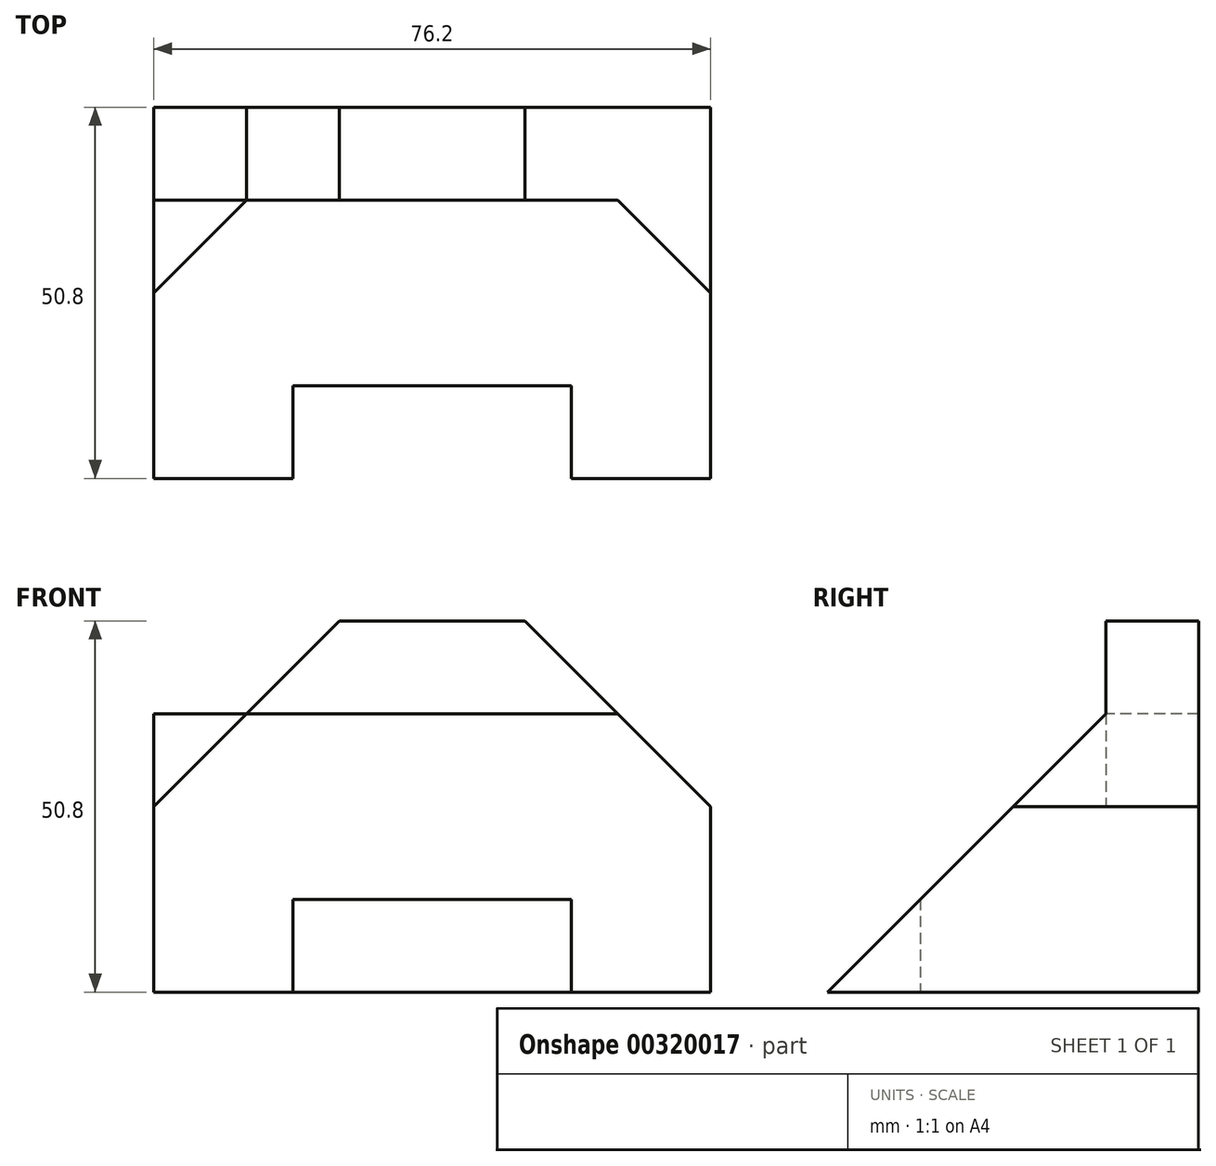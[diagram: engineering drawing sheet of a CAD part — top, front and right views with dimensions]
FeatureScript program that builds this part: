
annotation { "Feature Type Name" : "Feature", "Feature Type Description" : "" }
export const myFeature = defineFeature(function(context is Context, id is Id, definition is map)
    precondition{}
    {
        {
            var Q0;
            Q0=qCreatedBy(makeId("Top.planeOp"),FACE);
            var sketch = newSketch(context, id + "F0", { "sketchPlane" : qUnion([Q0])});
            skLineSegment(sketch, "E0", {"start": v(-38.1, 50.8) * mm, "end": v(-38.1, 0) * mm});
            skLineSegment(sketch, "E1", {"start": v(-38.1, 0) * mm, "end": v(-19.05, 0) * mm});
            skLineSegment(sketch, "E2", {"start": v(-19.05, 0) * mm, "end": v(-19.05, 12.7) * mm});
            skLineSegment(sketch, "E3", {"start": v(-19.05, 12.7) * mm, "end": v(19.05, 12.7) * mm});
            skLineSegment(sketch, "E4", {"start": v(19.05, 12.7) * mm, "end": v(19.05, 0) * mm});
            skLineSegment(sketch, "E5", {"start": v(19.05, 0) * mm, "end": v(38.1, 0) * mm});
            skLineSegment(sketch, "E6", {"start": v(38.1, 0) * mm, "end": v(38.1, 50.8) * mm});
            skLineSegment(sketch, "E7", {"start": v(38.1, 50.8) * mm, "end": v(-38.1, 50.8) * mm});
            skLineSegment(sketch, "E8", {"start": v(-38.1, 38.1) * mm, "end": v(38.1, 38.1) * mm});
            skLineSegment(sketch, "E9", {"start": v(-12.7, 50.8) * mm, "end": v(-12.7, 38.1) * mm});
            skLineSegment(sketch, "E10", {"start": v(12.7, 50.8) * mm, "end": v(12.7, 38.1) * mm});
            skLineSegment(sketch, "E11", {"start": v(0, 38.1) * mm, "end": v(-38.1, 0) * mm});
            skLineSegment(sketch, "E12", {"start": v(0, 38.1) * mm, "end": v(38.1, 0) * mm});
            skLineSegment(sketch, "E13", {"start": v(19.05, 0) * mm, "end": v(-19.05, 0) * mm, "construction": true});
            skSolve(sketch);
        }
        {
            var Q0;
            {var subQ5=sQuery(id+"F0.wireOp",EDGE,"E9");Q0=makeQuery(id+"F0.imprint","IMPRINT",FACE,{"disambiguationData":[TD([[makeQuery(id+"F0.imprint","IMPRINT",EDGE,{"derivedFrom":subQ5}),-1.0]])]});}
            var Q1;
            {var subQ0=sQuery(id+"F0.wireOp",EDGE,"E9");Q1=makeQuery(id+"F0.imprint","IMPRINT",FACE,{"disambiguationData":[TD([[makeQuery(id+"F0.imprint","IMPRINT",EDGE,{"derivedFrom":subQ0}),1.0]])]});}
            var Q2;
            {var subQ5=sQuery(id+"F0.wireOp",EDGE,"E10");Q2=makeQuery(id+"F0.imprint","IMPRINT",FACE,{"disambiguationData":[TD([[makeQuery(id+"F0.imprint","IMPRINT",EDGE,{"derivedFrom":subQ5}),1.0]])]});}
            extrude(context, id + "F1", {"entities" : qUnion([Q0, Q1, Q2]), "depth" : 50.8 * mm});
        }
        {
            var Q0;
            Q0=makeQuery(id+"F0.imprint","IMPRINT",FACE,{"disambiguationData":[TD([[makeQuery(id+"F0.imprint","IMPRINT",EDGE,{"derivedFrom":sQuery(id+"F0.wireOp",EDGE,"E1")}),1.0]])]});
            var Q1;
            {var subQ0=sQuery(id+"F0.wireOp",EDGE,"E12");Q1=makeQuery(id+"F0.imprint","IMPRINT",FACE,{"disambiguationData":[TD([[makeQuery(id+"F0.imprint","IMPRINT",EDGE,{"derivedFrom":subQ0}),1.0]])]});}
            var Q2;
            {var subQ0=sQuery(id+"F0.wireOp",EDGE,"E11");Q2=makeQuery(id+"F0.imprint","IMPRINT",FACE,{"disambiguationData":[TD([[makeQuery(id+"F0.imprint","IMPRINT",EDGE,{"derivedFrom":subQ0}),-1.0]])]});}
            extrude(context, id + "F2", {"entities" : qUnion([Q0, Q1, Q2]), "operationType" : NewBodyOperationType.ADD, "depth" : 38.1 * mm});
        }
        {
            var Q0;
            Q0=qCreatedBy(makeId("Front.planeOp"),FACE);
            var sketch = newSketch(context, id + "F3", { "sketchPlane" : qUnion([Q0])});
            skLineSegment(sketch, "E14.0.0", {"start": v(-38.1, 0) * mm, "end": v(-19.05, 0) * mm});
            skLineSegment(sketch, "E14.0.1", {"start": v(-19.05, 0) * mm, "end": v(-19.05, 38.1) * mm});
            skLineSegment(sketch, "E14.0.2", {"start": v(-19.05, 38.1) * mm, "end": v(-38.1, 38.1) * mm});
            skLineSegment(sketch, "E14.0.3", {"start": v(-38.1, 38.1) * mm, "end": v(-38.1, 0) * mm});
            skLineSegment(sketch, "E15.0.0", {"start": v(-19.05, 0) * mm, "end": v(19.05, 0) * mm});
            skLineSegment(sketch, "E15.0.1", {"start": v(19.05, 0) * mm, "end": v(19.05, 38.1) * mm});
            skLineSegment(sketch, "E15.0.2", {"start": v(19.05, 38.1) * mm, "end": v(-19.05, 38.1) * mm});
            skLineSegment(sketch, "E15.0.3", {"start": v(-19.05, 38.1) * mm, "end": v(-19.05, 0) * mm});
            skLineSegment(sketch, "E16.0.0", {"start": v(-38.1, 50.8) * mm, "end": v(-38.1, 38.1) * mm});
            skLineSegment(sketch, "E16.0.1", {"start": v(-38.1, 38.1) * mm, "end": v(38.1, 38.1) * mm});
            skLineSegment(sketch, "E16.0.2", {"start": v(38.1, 38.1) * mm, "end": v(38.1, 50.8) * mm});
            skLineSegment(sketch, "E16.0.3", {"start": v(38.1, 50.8) * mm, "end": v(-38.1, 50.8) * mm});
            skLineSegment(sketch, "E17.0.0", {"start": v(19.05, 0) * mm, "end": v(38.1, 0) * mm});
            skLineSegment(sketch, "E17.0.1", {"start": v(38.1, 0) * mm, "end": v(38.1, 38.1) * mm});
            skLineSegment(sketch, "E17.0.2", {"start": v(38.1, 38.1) * mm, "end": v(19.05, 38.1) * mm});
            skLineSegment(sketch, "E17.0.3", {"start": v(19.05, 38.1) * mm, "end": v(19.05, 0) * mm});
            skLineSegment(sketch, "E18", {"start": v(-12.7, 50.8) * mm, "end": v(-38.1, 25.4) * mm});
            skLineSegment(sketch, "E19", {"start": v(-38.1, 25.4) * mm, "end": v(-38.1, 50.8) * mm});
            skLineSegment(sketch, "E20", {"start": v(12.7, 50.8) * mm, "end": v(38.1, 25.4) * mm});
            skLineSegment(sketch, "E21", {"start": v(38.1, 25.4) * mm, "end": v(38.1, 50.8) * mm});
            skLineSegment(sketch, "E22", {"start": v(0, 38.1) * mm, "end": v(-38.1, 0) * mm});
            skLineSegment(sketch, "E23", {"start": v(0, 38.1) * mm, "end": v(38.1, 0) * mm});
            skSolve(sketch);
        }
        {
            var Q0;
            {var subQ0=sQuery(id+"F3.wireOp",EDGE,"E19");var subQ1=sQuery(id+"F3.wireOp",EDGE,"E16.0.1");var subQ2=makeQuery(id+"F3.imprint","INTERSECT",VERTEX,{"derivedFrom":[subQ1,subQ0]});Q0=makeQuery(id+"F3.imprint","IMPRINT",FACE,{"disambiguationData":[TD([[makeQuery(id+"F3.imprint","IMPRINT",EDGE,{"disambiguationData":[TD([[subQ2,-1.0]])],"derivedFrom":subQ1}),1.0]])]});}
            var Q1;
            {var subQ0=sQuery(id+"F3.wireOp",EDGE,"E19");var subQ1=sQuery(id+"F3.wireOp",EDGE,"E16.0.1");var subQ2=makeQuery(id+"F3.imprint","INTERSECT",VERTEX,{"derivedFrom":[subQ1,subQ0]});Q1=makeQuery(id+"F3.imprint","IMPRINT",FACE,{"disambiguationData":[TD([[makeQuery(id+"F3.imprint","IMPRINT",EDGE,{"disambiguationData":[TD([[subQ2,-1.0]])],"derivedFrom":subQ1}),-1.0]])]});}
            var Q2;
            {var subQ0=sQuery(id+"F3.wireOp",EDGE,"E21");var subQ1=sQuery(id+"F3.wireOp",EDGE,"E16.0.3");var subQ2=makeQuery(id+"F3.imprint","INTERSECT",VERTEX,{"derivedFrom":[subQ1,subQ0]});Q2=makeQuery(id+"F3.imprint","IMPRINT",FACE,{"disambiguationData":[TD([[makeQuery(id+"F3.imprint","IMPRINT",EDGE,{"disambiguationData":[TD([[subQ2,-1.0]])],"derivedFrom":subQ1}),1.0]])]});}
            var Q3;
            {var subQ0=sQuery(id+"F3.wireOp",EDGE,"E21");var subQ1=sQuery(id+"F3.wireOp",EDGE,"E17.0.2");var subQ2=makeQuery(id+"F3.imprint","INTERSECT",VERTEX,{"derivedFrom":[subQ1,subQ0]});Q3=makeQuery(id+"F3.imprint","IMPRINT",FACE,{"disambiguationData":[TD([[makeQuery(id+"F3.imprint","IMPRINT",EDGE,{"disambiguationData":[TD([[subQ2,-1.0]])],"derivedFrom":subQ1}),1.0]])]});}
            extrude(context, id + "F4", {"entities" : qUnion([Q0, Q1, Q2, Q3]), "operationType" : NewBodyOperationType.REMOVE, "endBound" : BoundingType.THROUGH_ALL, "oppositeDirection" : true, "depth" : 25.4 * mm});
        }
        {
            var Q0;
            {var subQ1=sQuery(id+"F3.wireOp",EDGE,"E14.0.3");Q0=makeQuery(id+"F3.imprint","IMPRINT",FACE,{"disambiguationData":[TD([[makeQuery(id+"F3.imprint","IMPRINT",EDGE,{"derivedFrom":subQ1}),1.0]])]});}
            var Q1;
            {var subQ7=sQuery(id+"F3.wireOp",EDGE,"E17.0.1");Q1=makeQuery(id+"F3.imprint","IMPRINT",FACE,{"disambiguationData":[TD([[makeQuery(id+"F3.imprint","IMPRINT",EDGE,{"derivedFrom":subQ7}),1.0]])]});}
            var Q2;
            {var subQ0=sQuery(id+"F3.wireOp",EDGE,"E17.0.3");var subQ3=sQuery(id+"F3.wireOp",EDGE,"E23");var subQ5=makeQuery(id+"F3.imprint","INTERSECT",VERTEX,{"derivedFrom":[subQ0,subQ3]});Q2=makeQuery(id+"F3.imprint","IMPRINT",FACE,{"disambiguationData":[TD([[makeQuery(id+"F3.imprint","IMPRINT",EDGE,{"disambiguationData":[TD([[subQ5,1.0]])],"derivedFrom":subQ0}),-1.0]])]});}
            var Q3;
            {var subQ0=sQuery(id+"F3.wireOp",EDGE,"E16.0.1");var subQ1=sQuery(id+"F3.wireOp",EDGE,"E15.0.3");var subQ2=makeQuery(id+"F3.imprint","INTERSECT",VERTEX,{"derivedFrom":[subQ1,subQ0]});Q3=makeQuery(id+"F3.imprint","IMPRINT",FACE,{"disambiguationData":[TD([[makeQuery(id+"F3.imprint","IMPRINT",EDGE,{"disambiguationData":[TD([[subQ2,-1.0]])],"derivedFrom":subQ1}),1.0]])]});}
            var Q4;
            Q4=makeQuery(id+"F1.opExtrude","SWEPT_FACE",FACE,{"disambiguationData":[OSD([sQuery(id+"F0.wireOp",EDGE,"E8")])]});
            extrude(context, id + "F5", {"entities" : qUnion([Q0, Q1, Q2, Q3]), "operationType" : NewBodyOperationType.REMOVE, "endBound" : BoundingType.UP_TO_SURFACE, "oppositeDirection" : true, "endBoundEntityFace" : qUnion([Q4]), "depth" : 25.4 * mm});
        }
        {
            var Q0;
            Q0=makeQuery(id+"F2.opExtrude","SWEPT_FACE",FACE,{"disambiguationData":[OSD([sQuery(id+"F0.wireOp",EDGE,"E3")])]});
            var sketch = newSketch(context, id + "F6", { "sketchPlane" : qUnion([Q0])});
            skLineSegment(sketch, "E24", {"start": v(19.05, 0) * mm, "end": v(-19.05, 0) * mm});
            skLineSegment(sketch, "E25", {"start": v(-19.05, 0) * mm, "end": v(-19.05, 12.7) * mm});
            skLineSegment(sketch, "E26", {"start": v(-19.05, 12.7) * mm, "end": v(19.05, 12.7) * mm});
            skLineSegment(sketch, "E27", {"start": v(19.05, 12.7) * mm, "end": v(19.05, 0) * mm});
            skSolve(sketch);
        }
        {
            var Q0;
            {var subQ5=sQuery(id+"F6.wireOp",EDGE,"E26");Q0=makeQuery(id+"F6.imprint","IMPRINT",FACE,{"disambiguationData":[TD([[makeQuery(id+"F6.imprint","IMPRINT",EDGE,{"derivedFrom":subQ5}),1.0]])]});}
            var Q1;
            Q1=makeQuery(id+"F2.opExtrude","SWEPT_FACE",FACE,{"disambiguationData":[OSD([sQuery(id+"F0.wireOp",EDGE,"E5")])]});
            extrude(context, id + "F7", {"entities" : qUnion([Q0]), "operationType" : NewBodyOperationType.ADD, "endBound" : BoundingType.UP_TO_SURFACE, "endBoundEntityFace" : qUnion([Q1]), "depth" : 25.4 * mm});
        }
        {
            var Q0;
            Q0=qCreatedBy(makeId("Right.planeOp"),FACE);
            var sketch = newSketch(context, id + "F8", { "sketchPlane" : qUnion([Q0])});
            skLineSegment(sketch, "E28.0.0", {"start": v(38.1, 38.1) * mm, "end": v(0, 38.1) * mm});
            skLineSegment(sketch, "E28.0.1", {"start": v(0, 38.1) * mm, "end": v(0, 0) * mm});
            skLineSegment(sketch, "E28.0.2", {"start": v(0, 0) * mm, "end": v(38.1, 0) * mm});
            skLineSegment(sketch, "E28.0.3", {"start": v(38.1, 0) * mm, "end": v(38.1, 38.1) * mm});
            skLineSegment(sketch, "E29", {"start": v(38.1, 38.1) * mm, "end": v(0, 0) * mm});
            skLineSegment(sketch, "E30", {"start": v(0, 38.1) * mm, "end": v(38.1, 38.1) * mm});
            skSolve(sketch);
        }
        {
            var Q0;
            Q0=makeQuery(id+"F8.imprint","IMPRINT",FACE,{"disambiguationData":[TD([[makeQuery(id+"F8.imprint","IMPRINT",EDGE,{"derivedFrom":sQuery(id+"F8.wireOp",EDGE,"E28.0.1")}),1.0]])]});
            extrude(context, id + "F9", {"entities" : qUnion([Q0]), "operationType" : NewBodyOperationType.REMOVE, "endBound" : BoundingType.THROUGH_ALL, "oppositeDirection" : true, "depth" : 25.4 * mm, "hasSecondDirection" : true, "secondDirectionBound" : BoundingType.THROUGH_ALL, "secondDirectionOppositeDirection" : false, "secondDirectionDepth" : 25.4 * mm});
        }
    });
